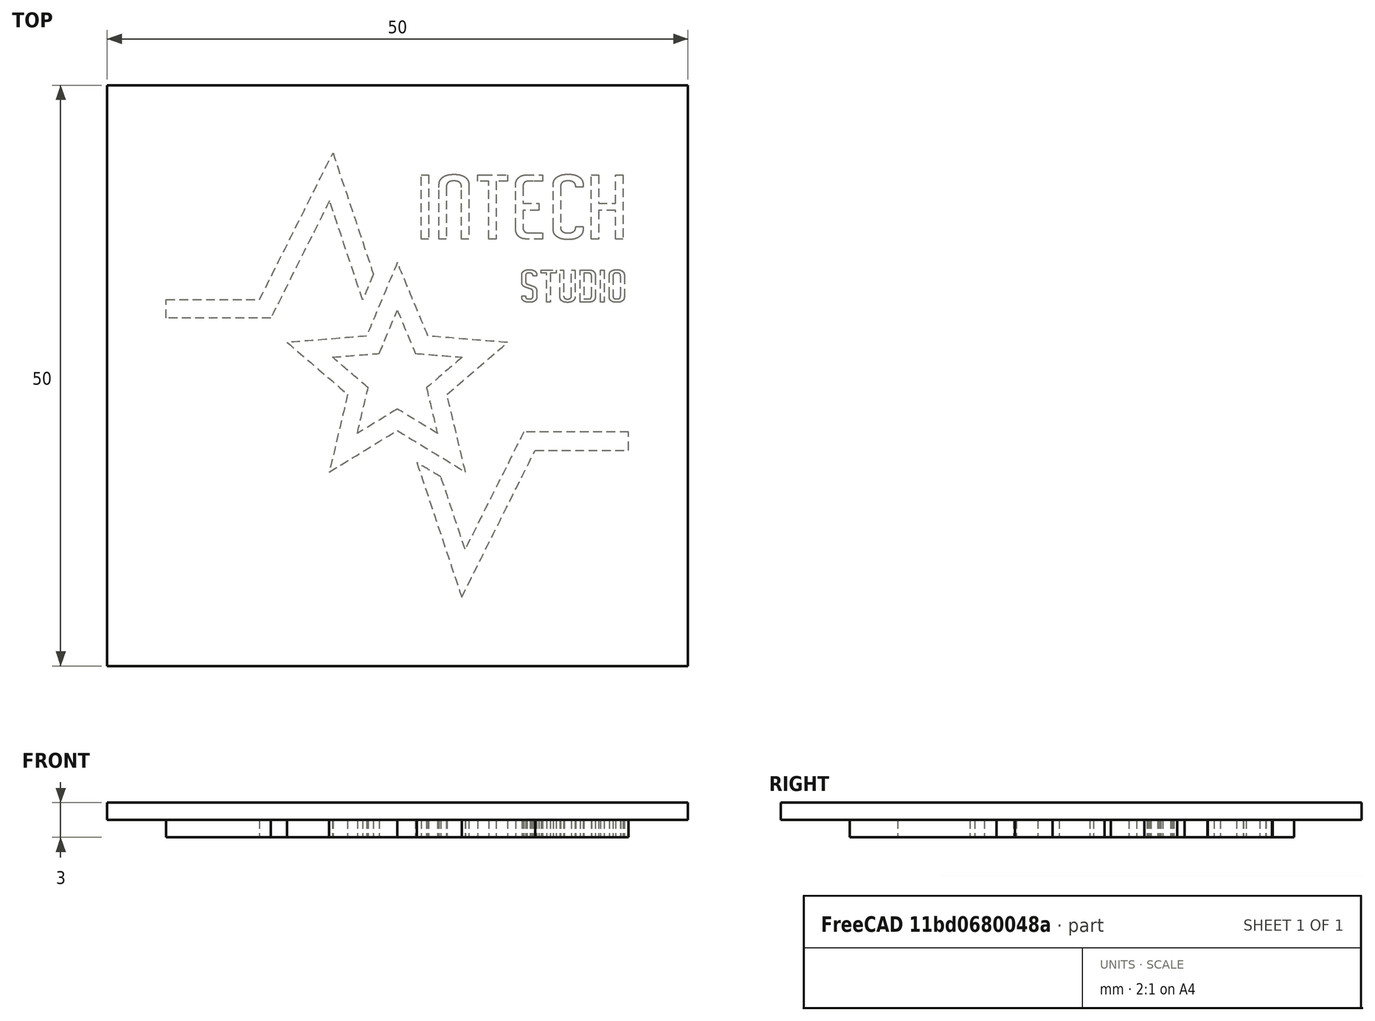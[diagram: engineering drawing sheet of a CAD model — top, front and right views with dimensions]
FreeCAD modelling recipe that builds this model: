
FCSTD DOCUMENT  (FreeCAD 0.18R16131 (Git))
Label: Intech Logo 5cm
License: All rights reserved
LicenseURL: http://en.wikipedia.org/wiki/All_rights_reserved
objects: Sketcher::SketchObject×2, PartDesign::Pad×2, PartDesign::Body×1
note: 7 computed .brp shape members not serialized (recipe doc carries the construction recipe); baked Part::Feature solids carry a one-line shape summary decoded from their .brp

FEATURE [Sketcher::SketchObject] Sketch018
  sketch-geometry (348):
    g0: BSplineCurve PolesCount=2 KnotsCount=2 Degree=1 IsPeriodic=0
    g1: BSplineCurve PolesCount=2 KnotsCount=2 Degree=1 IsPeriodic=0
    g2: BSplineCurve PolesCount=2 KnotsCount=2 Degree=1 IsPeriodic=0
    g3: BSplineCurve PolesCount=2 KnotsCount=2 Degree=1 IsPeriodic=0
    g4: BSplineCurve PolesCount=4 KnotsCount=2 Degree=3 IsPeriodic=0
    g5: BSplineCurve PolesCount=4 KnotsCount=2 Degree=3 IsPeriodic=0
    g6: BSplineCurve PolesCount=4 KnotsCount=2 Degree=3 IsPeriodic=0
    g7: BSplineCurve PolesCount=4 KnotsCount=2 Degree=3 IsPeriodic=0
    g8: BSplineCurve PolesCount=4 KnotsCount=2 Degree=3 IsPeriodic=0
    g9: BSplineCurve PolesCount=4 KnotsCount=2 Degree=3 IsPeriodic=0
    g10: BSplineCurve PolesCount=4 KnotsCount=2 Degree=3 IsPeriodic=0
    g11: BSplineCurve PolesCount=4 KnotsCount=2 Degree=3 IsPeriodic=0
    g12: BSplineCurve PolesCount=2 KnotsCount=2 Degree=1 IsPeriodic=0
    g13: BSplineCurve PolesCount=2 KnotsCount=2 Degree=1 IsPeriodic=0
    g14: BSplineCurve PolesCount=2 KnotsCount=2 Degree=1 IsPeriodic=0
    g15: BSplineCurve PolesCount=4 KnotsCount=2 Degree=3 IsPeriodic=0
    g16: BSplineCurve PolesCount=4 KnotsCount=2 Degree=3 IsPeriodic=0
    g17: BSplineCurve PolesCount=4 KnotsCount=2 Degree=3 IsPeriodic=0
    g18: BSplineCurve PolesCount=4 KnotsCount=2 Degree=3 IsPeriodic=0
    g19: BSplineCurve PolesCount=4 KnotsCount=2 Degree=3 IsPeriodic=0
    g20: BSplineCurve PolesCount=4 KnotsCount=2 Degree=3 IsPeriodic=0
    g21: BSplineCurve PolesCount=4 KnotsCount=2 Degree=3 IsPeriodic=0
    g22: BSplineCurve PolesCount=4 KnotsCount=2 Degree=3 IsPeriodic=0
    g23: BSplineCurve PolesCount=2 KnotsCount=2 Degree=1 IsPeriodic=0
    g24: BSplineCurve PolesCount=2 KnotsCount=2 Degree=1 IsPeriodic=0
    g25: BSplineCurve PolesCount=2 KnotsCount=2 Degree=1 IsPeriodic=0
    g26: BSplineCurve PolesCount=2 KnotsCount=2 Degree=1 IsPeriodic=0
    g27: BSplineCurve PolesCount=2 KnotsCount=2 Degree=1 IsPeriodic=0
    g28: BSplineCurve PolesCount=2 KnotsCount=2 Degree=1 IsPeriodic=0
    g29: BSplineCurve PolesCount=2 KnotsCount=2 Degree=1 IsPeriodic=0
    g30: BSplineCurve PolesCount=2 KnotsCount=2 Degree=1 IsPeriodic=0
    g31: BSplineCurve PolesCount=2 KnotsCount=2 Degree=1 IsPeriodic=0
    g32: BSplineCurve PolesCount=2 KnotsCount=2 Degree=1 IsPeriodic=0
    g33: BSplineCurve PolesCount=2 KnotsCount=2 Degree=1 IsPeriodic=0
    g34: BSplineCurve PolesCount=2 KnotsCount=2 Degree=1 IsPeriodic=0
    g35: BSplineCurve PolesCount=2 KnotsCount=2 Degree=1 IsPeriodic=0
    g36: BSplineCurve PolesCount=2 KnotsCount=2 Degree=1 IsPeriodic=0
    g37: BSplineCurve PolesCount=2 KnotsCount=2 Degree=1 IsPeriodic=0
    g38: BSplineCurve PolesCount=2 KnotsCount=2 Degree=1 IsPeriodic=0
    g39: BSplineCurve PolesCount=2 KnotsCount=2 Degree=1 IsPeriodic=0
    g40: BSplineCurve PolesCount=2 KnotsCount=2 Degree=1 IsPeriodic=0
    g41: BSplineCurve PolesCount=2 KnotsCount=2 Degree=1 IsPeriodic=0
    g42: BSplineCurve PolesCount=2 KnotsCount=2 Degree=1 IsPeriodic=0
    g43: BSplineCurve PolesCount=2 KnotsCount=2 Degree=1 IsPeriodic=0
    g44: BSplineCurve PolesCount=2 KnotsCount=2 Degree=1 IsPeriodic=0
    g45: BSplineCurve PolesCount=2 KnotsCount=2 Degree=1 IsPeriodic=0
    g46: BSplineCurve PolesCount=2 KnotsCount=2 Degree=1 IsPeriodic=0
    g47: BSplineCurve PolesCount=2 KnotsCount=2 Degree=1 IsPeriodic=0
    g48: BSplineCurve PolesCount=2 KnotsCount=2 Degree=1 IsPeriodic=0
    g49: BSplineCurve PolesCount=2 KnotsCount=2 Degree=1 IsPeriodic=0
    g50: BSplineCurve PolesCount=2 KnotsCount=2 Degree=1 IsPeriodic=0
    g51: BSplineCurve PolesCount=2 KnotsCount=2 Degree=1 IsPeriodic=0
    g52: BSplineCurve PolesCount=2 KnotsCount=2 Degree=1 IsPeriodic=0
    g53: BSplineCurve PolesCount=2 KnotsCount=2 Degree=1 IsPeriodic=0
    g54: BSplineCurve PolesCount=2 KnotsCount=2 Degree=1 IsPeriodic=0
    g55: BSplineCurve PolesCount=2 KnotsCount=2 Degree=1 IsPeriodic=0
    g56: BSplineCurve PolesCount=4 KnotsCount=2 Degree=3 IsPeriodic=0
    g57: BSplineCurve PolesCount=4 KnotsCount=2 Degree=3 IsPeriodic=0
    g58: BSplineCurve PolesCount=4 KnotsCount=2 Degree=3 IsPeriodic=0
    g59: BSplineCurve PolesCount=4 KnotsCount=2 Degree=3 IsPeriodic=0
    g60: BSplineCurve PolesCount=4 KnotsCount=2 Degree=3 IsPeriodic=0
    g61: BSplineCurve PolesCount=4 KnotsCount=2 Degree=3 IsPeriodic=0
    g62: BSplineCurve PolesCount=4 KnotsCount=2 Degree=3 IsPeriodic=0
    g63: BSplineCurve PolesCount=4 KnotsCount=2 Degree=3 IsPeriodic=0
    g64: BSplineCurve PolesCount=2 KnotsCount=2 Degree=1 IsPeriodic=0
    g65: BSplineCurve PolesCount=2 KnotsCount=2 Degree=1 IsPeriodic=0
    g66: BSplineCurve PolesCount=2 KnotsCount=2 Degree=1 IsPeriodic=0
    g67: BSplineCurve PolesCount=4 KnotsCount=2 Degree=3 IsPeriodic=0
    g68: BSplineCurve PolesCount=4 KnotsCount=2 Degree=3 IsPeriodic=0
    g69: BSplineCurve PolesCount=4 KnotsCount=2 Degree=3 IsPeriodic=0
    g70: BSplineCurve PolesCount=4 KnotsCount=2 Degree=3 IsPeriodic=0
    g71: BSplineCurve PolesCount=4 KnotsCount=2 Degree=3 IsPeriodic=0
    g72: BSplineCurve PolesCount=4 KnotsCount=2 Degree=3 IsPeriodic=0
    g73: BSplineCurve PolesCount=4 KnotsCount=2 Degree=3 IsPeriodic=0
    g74: BSplineCurve PolesCount=4 KnotsCount=2 Degree=3 IsPeriodic=0
    g75: BSplineCurve PolesCount=2 KnotsCount=2 Degree=1 IsPeriodic=0
    g76: BSplineCurve PolesCount=2 KnotsCount=2 Degree=1 IsPeriodic=0
    g77: BSplineCurve PolesCount=2 KnotsCount=2 Degree=1 IsPeriodic=0
    g78: BSplineCurve PolesCount=4 KnotsCount=2 Degree=3 IsPeriodic=0
    g79: BSplineCurve PolesCount=4 KnotsCount=2 Degree=3 IsPeriodic=0
    g80: BSplineCurve PolesCount=4 KnotsCount=2 Degree=3 IsPeriodic=0
    g81: BSplineCurve PolesCount=4 KnotsCount=2 Degree=3 IsPeriodic=0
    g82: BSplineCurve PolesCount=2 KnotsCount=2 Degree=1 IsPeriodic=0
    g83: BSplineCurve PolesCount=4 KnotsCount=2 Degree=3 IsPeriodic=0
    g84: BSplineCurve PolesCount=4 KnotsCount=2 Degree=3 IsPeriodic=0
    g85: BSplineCurve PolesCount=4 KnotsCount=2 Degree=3 IsPeriodic=0
    g86: BSplineCurve PolesCount=2 KnotsCount=2 Degree=1 IsPeriodic=0
    g87: BSplineCurve PolesCount=2 KnotsCount=2 Degree=1 IsPeriodic=0
    g88: BSplineCurve PolesCount=2 KnotsCount=2 Degree=1 IsPeriodic=0
    g89: BSplineCurve PolesCount=2 KnotsCount=2 Degree=1 IsPeriodic=0
    g90: BSplineCurve PolesCount=4 KnotsCount=2 Degree=3 IsPeriodic=0
    g91: BSplineCurve PolesCount=4 KnotsCount=2 Degree=3 IsPeriodic=0
    g92: BSplineCurve PolesCount=4 KnotsCount=2 Degree=3 IsPeriodic=0
    g93: BSplineCurve PolesCount=4 KnotsCount=2 Degree=3 IsPeriodic=0
    g94: BSplineCurve PolesCount=4 KnotsCount=2 Degree=3 IsPeriodic=0
    g95: BSplineCurve PolesCount=4 KnotsCount=2 Degree=3 IsPeriodic=0
    g96: BSplineCurve PolesCount=4 KnotsCount=2 Degree=3 IsPeriodic=0
    g97: BSplineCurve PolesCount=4 KnotsCount=2 Degree=3 IsPeriodic=0
    g98: BSplineCurve PolesCount=2 KnotsCount=2 Degree=1 IsPeriodic=0
    g99: BSplineCurve PolesCount=2 KnotsCount=2 Degree=1 IsPeriodic=0
    g100: BSplineCurve PolesCount=2 KnotsCount=2 Degree=1 IsPeriodic=0
    g101: BSplineCurve PolesCount=4 KnotsCount=2 Degree=3 IsPeriodic=0
    g102: BSplineCurve PolesCount=4 KnotsCount=2 Degree=3 IsPeriodic=0
    g103: BSplineCurve PolesCount=4 KnotsCount=2 Degree=3 IsPeriodic=0
    g104: BSplineCurve PolesCount=4 KnotsCount=2 Degree=3 IsPeriodic=0
    g105: BSplineCurve PolesCount=4 KnotsCount=2 Degree=3 IsPeriodic=0
    g106: BSplineCurve PolesCount=4 KnotsCount=2 Degree=3 IsPeriodic=0
    g107: BSplineCurve PolesCount=4 KnotsCount=2 Degree=3 IsPeriodic=0
    g108: BSplineCurve PolesCount=4 KnotsCount=2 Degree=3 IsPeriodic=0
    g109: BSplineCurve PolesCount=2 KnotsCount=2 Degree=1 IsPeriodic=0
    g110: BSplineCurve PolesCount=2 KnotsCount=2 Degree=1 IsPeriodic=0
    g111: BSplineCurve PolesCount=2 KnotsCount=2 Degree=1 IsPeriodic=0
    g112: BSplineCurve PolesCount=4 KnotsCount=2 Degree=3 IsPeriodic=0
    g113: BSplineCurve PolesCount=4 KnotsCount=2 Degree=3 IsPeriodic=0
    g114: BSplineCurve PolesCount=4 KnotsCount=2 Degree=3 IsPeriodic=0
    g115: BSplineCurve PolesCount=4 KnotsCount=2 Degree=3 IsPeriodic=0
    g116: BSplineCurve PolesCount=4 KnotsCount=2 Degree=3 IsPeriodic=0
    g117: BSplineCurve PolesCount=4 KnotsCount=2 Degree=3 IsPeriodic=0
    g118: BSplineCurve PolesCount=4 KnotsCount=2 Degree=3 IsPeriodic=0
    g119: BSplineCurve PolesCount=4 KnotsCount=2 Degree=3 IsPeriodic=0
    g120: BSplineCurve PolesCount=4 KnotsCount=2 Degree=3 IsPeriodic=0
    g121: BSplineCurve PolesCount=4 KnotsCount=2 Degree=3 IsPeriodic=0
    g122: BSplineCurve PolesCount=2 KnotsCount=2 Degree=1 IsPeriodic=0
    g123: BSplineCurve PolesCount=2 KnotsCount=2 Degree=1 IsPeriodic=0
    g124: BSplineCurve PolesCount=2 KnotsCount=2 Degree=1 IsPeriodic=0
    g125: BSplineCurve PolesCount=2 KnotsCount=2 Degree=1 IsPeriodic=0
    g126: BSplineCurve PolesCount=2 KnotsCount=2 Degree=1 IsPeriodic=0
    g127: BSplineCurve PolesCount=2 KnotsCount=2 Degree=1 IsPeriodic=0
    g128: BSplineCurve PolesCount=4 KnotsCount=2 Degree=3 IsPeriodic=0
    g129: BSplineCurve PolesCount=4 KnotsCount=2 Degree=3 IsPeriodic=0
    g130: BSplineCurve PolesCount=4 KnotsCount=2 Degree=3 IsPeriodic=0
    g131: BSplineCurve PolesCount=4 KnotsCount=2 Degree=3 IsPeriodic=0
    g132: BSplineCurve PolesCount=4 KnotsCount=2 Degree=3 IsPeriodic=0
    g133: BSplineCurve PolesCount=4 KnotsCount=2 Degree=3 IsPeriodic=0
    g134: BSplineCurve PolesCount=4 KnotsCount=2 Degree=3 IsPeriodic=0
    g135: BSplineCurve PolesCount=4 KnotsCount=2 Degree=3 IsPeriodic=0
    g136: BSplineCurve PolesCount=2 KnotsCount=2 Degree=1 IsPeriodic=0
    g137: BSplineCurve PolesCount=2 KnotsCount=2 Degree=1 IsPeriodic=0
    g138: BSplineCurve PolesCount=2 KnotsCount=2 Degree=1 IsPeriodic=0
    g139: BSplineCurve PolesCount=2 KnotsCount=2 Degree=1 IsPeriodic=0
    g140: BSplineCurve PolesCount=2 KnotsCount=2 Degree=1 IsPeriodic=0
    g141: BSplineCurve PolesCount=4 KnotsCount=2 Degree=3 IsPeriodic=0
    g142: BSplineCurve PolesCount=4 KnotsCount=2 Degree=3 IsPeriodic=0
    g143: BSplineCurve PolesCount=4 KnotsCount=2 Degree=3 IsPeriodic=0
    g144: BSplineCurve PolesCount=4 KnotsCount=2 Degree=3 IsPeriodic=0
    g145: BSplineCurve PolesCount=4 KnotsCount=2 Degree=3 IsPeriodic=0
    g146: BSplineCurve PolesCount=4 KnotsCount=2 Degree=3 IsPeriodic=0
    g147: BSplineCurve PolesCount=4 KnotsCount=2 Degree=3 IsPeriodic=0
    g148: BSplineCurve PolesCount=4 KnotsCount=2 Degree=3 IsPeriodic=0
    g149: BSplineCurve PolesCount=2 KnotsCount=2 Degree=1 IsPeriodic=0
    g150: BSplineCurve PolesCount=2 KnotsCount=2 Degree=1 IsPeriodic=0
    g151: BSplineCurve PolesCount=2 KnotsCount=2 Degree=1 IsPeriodic=0
    g152: BSplineCurve PolesCount=2 KnotsCount=2 Degree=1 IsPeriodic=0
    g153: BSplineCurve PolesCount=2 KnotsCount=2 Degree=1 IsPeriodic=0
    g154: BSplineCurve PolesCount=2 KnotsCount=2 Degree=1 IsPeriodic=0
    g155: BSplineCurve PolesCount=2 KnotsCount=2 Degree=1 IsPeriodic=0
    g156: BSplineCurve PolesCount=2 KnotsCount=2 Degree=1 IsPeriodic=0
    g157: BSplineCurve PolesCount=2 KnotsCount=2 Degree=1 IsPeriodic=0
    g158: BSplineCurve PolesCount=2 KnotsCount=2 Degree=1 IsPeriodic=0
    g159: BSplineCurve PolesCount=2 KnotsCount=2 Degree=1 IsPeriodic=0
    g160: BSplineCurve PolesCount=2 KnotsCount=2 Degree=1 IsPeriodic=0
    g161: BSplineCurve PolesCount=2 KnotsCount=2 Degree=1 IsPeriodic=0
    g162: BSplineCurve PolesCount=2 KnotsCount=2 Degree=1 IsPeriodic=0
    g163: BSplineCurve PolesCount=2 KnotsCount=2 Degree=1 IsPeriodic=0
    g164: BSplineCurve PolesCount=4 KnotsCount=2 Degree=3 IsPeriodic=0
    g165: BSplineCurve PolesCount=4 KnotsCount=2 Degree=3 IsPeriodic=0
    g166: BSplineCurve PolesCount=4 KnotsCount=2 Degree=3 IsPeriodic=0
    g167: BSplineCurve PolesCount=4 KnotsCount=2 Degree=3 IsPeriodic=0
    g168: BSplineCurve PolesCount=4 KnotsCount=2 Degree=3 IsPeriodic=0
    g169: BSplineCurve PolesCount=4 KnotsCount=2 Degree=3 IsPeriodic=0
    g170: BSplineCurve PolesCount=4 KnotsCount=2 Degree=3 IsPeriodic=0
    g171: BSplineCurve PolesCount=4 KnotsCount=2 Degree=3 IsPeriodic=0
    g172: BSplineCurve PolesCount=2 KnotsCount=2 Degree=1 IsPeriodic=0
    g173: BSplineCurve PolesCount=2 KnotsCount=2 Degree=1 IsPeriodic=0
    g174: BSplineCurve PolesCount=2 KnotsCount=2 Degree=1 IsPeriodic=0
    g175: BSplineCurve PolesCount=2 KnotsCount=2 Degree=1 IsPeriodic=0
    g176: BSplineCurve PolesCount=2 KnotsCount=2 Degree=1 IsPeriodic=0
    g177: BSplineCurve PolesCount=4 KnotsCount=2 Degree=3 IsPeriodic=0
    g178: BSplineCurve PolesCount=4 KnotsCount=2 Degree=3 IsPeriodic=0
    g179: BSplineCurve PolesCount=4 KnotsCount=2 Degree=3 IsPeriodic=0
    g180: BSplineCurve PolesCount=4 KnotsCount=2 Degree=3 IsPeriodic=0
    g181: BSplineCurve PolesCount=4 KnotsCount=2 Degree=3 IsPeriodic=0
    g182: BSplineCurve PolesCount=4 KnotsCount=2 Degree=3 IsPeriodic=0
    g183: BSplineCurve PolesCount=4 KnotsCount=2 Degree=3 IsPeriodic=0
    g184: BSplineCurve PolesCount=4 KnotsCount=2 Degree=3 IsPeriodic=0
    g185: BSplineCurve PolesCount=2 KnotsCount=2 Degree=1 IsPeriodic=0
    g186: BSplineCurve PolesCount=2 KnotsCount=2 Degree=1 IsPeriodic=0
    g187: BSplineCurve PolesCount=2 KnotsCount=2 Degree=1 IsPeriodic=0
    g188: BSplineCurve PolesCount=2 KnotsCount=2 Degree=1 IsPeriodic=0
    g189: BSplineCurve PolesCount=2 KnotsCount=2 Degree=1 IsPeriodic=0
    g190: BSplineCurve PolesCount=4 KnotsCount=2 Degree=3 IsPeriodic=0
    g191: BSplineCurve PolesCount=4 KnotsCount=2 Degree=3 IsPeriodic=0
    g192: BSplineCurve PolesCount=4 KnotsCount=2 Degree=3 IsPeriodic=0
    g193: BSplineCurve PolesCount=4 KnotsCount=2 Degree=3 IsPeriodic=0
    g194: BSplineCurve PolesCount=2 KnotsCount=2 Degree=1 IsPeriodic=0
    g195: BSplineCurve PolesCount=2 KnotsCount=2 Degree=1 IsPeriodic=0
    g196: BSplineCurve PolesCount=2 KnotsCount=2 Degree=1 IsPeriodic=0
    g197: BSplineCurve PolesCount=4 KnotsCount=2 Degree=3 IsPeriodic=0
    g198: BSplineCurve PolesCount=4 KnotsCount=2 Degree=3 IsPeriodic=0
    g199: BSplineCurve PolesCount=4 KnotsCount=2 Degree=3 IsPeriodic=0
    g200: BSplineCurve PolesCount=4 KnotsCount=2 Degree=3 IsPeriodic=0
    g201: BSplineCurve PolesCount=2 KnotsCount=2 Degree=1 IsPeriodic=0
    g202: BSplineCurve PolesCount=2 KnotsCount=2 Degree=1 IsPeriodic=0
    g203: BSplineCurve PolesCount=2 KnotsCount=2 Degree=1 IsPeriodic=0
    g204: BSplineCurve PolesCount=2 KnotsCount=2 Degree=1 IsPeriodic=0
    g205: BSplineCurve PolesCount=4 KnotsCount=2 Degree=3 IsPeriodic=0
    g206: BSplineCurve PolesCount=4 KnotsCount=2 Degree=3 IsPeriodic=0
    g207: BSplineCurve PolesCount=2 KnotsCount=2 Degree=1 IsPeriodic=0
    g208: BSplineCurve PolesCount=2 KnotsCount=2 Degree=1 IsPeriodic=0
    g209: BSplineCurve PolesCount=2 KnotsCount=2 Degree=1 IsPeriodic=0
    g210: BSplineCurve PolesCount=2 KnotsCount=2 Degree=1 IsPeriodic=0
    g211: BSplineCurve PolesCount=2 KnotsCount=2 Degree=1 IsPeriodic=0
    g212: BSplineCurve PolesCount=2 KnotsCount=2 Degree=1 IsPeriodic=0
    g213: BSplineCurve PolesCount=2 KnotsCount=2 Degree=1 IsPeriodic=0
    g214: BSplineCurve PolesCount=4 KnotsCount=2 Degree=3 IsPeriodic=0
    g215: BSplineCurve PolesCount=4 KnotsCount=2 Degree=3 IsPeriodic=0
    g216: BSplineCurve PolesCount=2 KnotsCount=2 Degree=1 IsPeriodic=0
    g217: BSplineCurve PolesCount=2 KnotsCount=2 Degree=1 IsPeriodic=0
    g218: BSplineCurve PolesCount=2 KnotsCount=2 Degree=1 IsPeriodic=0
    g219: BSplineCurve PolesCount=2 KnotsCount=2 Degree=1 IsPeriodic=0
    g220: BSplineCurve PolesCount=2 KnotsCount=2 Degree=1 IsPeriodic=0
    g221: BSplineCurve PolesCount=2 KnotsCount=2 Degree=1 IsPeriodic=0
    g222: BSplineCurve PolesCount=2 KnotsCount=2 Degree=1 IsPeriodic=0
    g223: BSplineCurve PolesCount=2 KnotsCount=2 Degree=1 IsPeriodic=0
    g224: BSplineCurve PolesCount=4 KnotsCount=2 Degree=3 IsPeriodic=0
    g225: BSplineCurve PolesCount=4 KnotsCount=2 Degree=3 IsPeriodic=0
    g226: BSplineCurve PolesCount=4 KnotsCount=2 Degree=3 IsPeriodic=0
    g227: BSplineCurve PolesCount=4 KnotsCount=2 Degree=3 IsPeriodic=0
    g228: BSplineCurve PolesCount=4 KnotsCount=2 Degree=3 IsPeriodic=0
    g229: BSplineCurve PolesCount=4 KnotsCount=2 Degree=3 IsPeriodic=0
    g230: BSplineCurve PolesCount=4 KnotsCount=2 Degree=3 IsPeriodic=0
    g231: BSplineCurve PolesCount=4 KnotsCount=2 Degree=3 IsPeriodic=0
    g232: BSplineCurve PolesCount=2 KnotsCount=2 Degree=1 IsPeriodic=0
    g233: BSplineCurve PolesCount=2 KnotsCount=2 Degree=1 IsPeriodic=0
    g234: BSplineCurve PolesCount=2 KnotsCount=2 Degree=1 IsPeriodic=0
    g235: BSplineCurve PolesCount=4 KnotsCount=2 Degree=3 IsPeriodic=0
    g236: BSplineCurve PolesCount=4 KnotsCount=2 Degree=3 IsPeriodic=0
    g237: BSplineCurve PolesCount=4 KnotsCount=2 Degree=3 IsPeriodic=0
    g238: BSplineCurve PolesCount=4 KnotsCount=2 Degree=3 IsPeriodic=0
    g239: BSplineCurve PolesCount=4 KnotsCount=2 Degree=3 IsPeriodic=0
    g240: BSplineCurve PolesCount=4 KnotsCount=2 Degree=3 IsPeriodic=0
    g241: BSplineCurve PolesCount=4 KnotsCount=2 Degree=3 IsPeriodic=0
    g242: BSplineCurve PolesCount=4 KnotsCount=2 Degree=3 IsPeriodic=0
    g243: BSplineCurve PolesCount=2 KnotsCount=2 Degree=1 IsPeriodic=0
    g244: BSplineCurve PolesCount=2 KnotsCount=2 Degree=1 IsPeriodic=0
    g245: BSplineCurve PolesCount=2 KnotsCount=2 Degree=1 IsPeriodic=0
    g246: BSplineCurve PolesCount=4 KnotsCount=2 Degree=3 IsPeriodic=0
    g247: BSplineCurve PolesCount=4 KnotsCount=2 Degree=3 IsPeriodic=0
    g248: BSplineCurve PolesCount=4 KnotsCount=2 Degree=3 IsPeriodic=0
    g249: BSplineCurve PolesCount=4 KnotsCount=2 Degree=3 IsPeriodic=0
    g250: BSplineCurve PolesCount=4 KnotsCount=2 Degree=3 IsPeriodic=0
    g251: BSplineCurve PolesCount=4 KnotsCount=2 Degree=3 IsPeriodic=0
    g252: BSplineCurve PolesCount=4 KnotsCount=2 Degree=3 IsPeriodic=0
    g253: BSplineCurve PolesCount=4 KnotsCount=2 Degree=3 IsPeriodic=0
    g254: BSplineCurve PolesCount=2 KnotsCount=2 Degree=1 IsPeriodic=0
    g255: BSplineCurve PolesCount=2 KnotsCount=2 Degree=1 IsPeriodic=0
    g256: BSplineCurve PolesCount=2 KnotsCount=2 Degree=1 IsPeriodic=0
    g257: BSplineCurve PolesCount=4 KnotsCount=2 Degree=3 IsPeriodic=0
    g258: BSplineCurve PolesCount=4 KnotsCount=2 Degree=3 IsPeriodic=0
    g259: BSplineCurve PolesCount=4 KnotsCount=2 Degree=3 IsPeriodic=0
    g260: BSplineCurve PolesCount=4 KnotsCount=2 Degree=3 IsPeriodic=0
    g261: BSplineCurve PolesCount=4 KnotsCount=2 Degree=3 IsPeriodic=0
    g262: BSplineCurve PolesCount=4 KnotsCount=2 Degree=3 IsPeriodic=0
    g263: BSplineCurve PolesCount=4 KnotsCount=2 Degree=3 IsPeriodic=0
    g264: BSplineCurve PolesCount=4 KnotsCount=2 Degree=3 IsPeriodic=0
    g265: BSplineCurve PolesCount=2 KnotsCount=2 Degree=1 IsPeriodic=0
    g266: BSplineCurve PolesCount=2 KnotsCount=2 Degree=1 IsPeriodic=0
    g267: BSplineCurve PolesCount=2 KnotsCount=2 Degree=1 IsPeriodic=0
    g268: BSplineCurve PolesCount=2 KnotsCount=2 Degree=1 IsPeriodic=0
    g269: BSplineCurve PolesCount=2 KnotsCount=2 Degree=1 IsPeriodic=0
    g270: BSplineCurve PolesCount=2 KnotsCount=2 Degree=1 IsPeriodic=0
    g271: BSplineCurve PolesCount=2 KnotsCount=2 Degree=1 IsPeriodic=0
    g272: BSplineCurve PolesCount=2 KnotsCount=2 Degree=1 IsPeriodic=0
    g273: BSplineCurve PolesCount=2 KnotsCount=2 Degree=1 IsPeriodic=0
    g274: BSplineCurve PolesCount=2 KnotsCount=2 Degree=1 IsPeriodic=0
    g275: BSplineCurve PolesCount=2 KnotsCount=2 Degree=1 IsPeriodic=0
    g276: BSplineCurve PolesCount=2 KnotsCount=2 Degree=1 IsPeriodic=0
    g277: BSplineCurve PolesCount=2 KnotsCount=2 Degree=1 IsPeriodic=0
    g278: BSplineCurve PolesCount=2 KnotsCount=2 Degree=1 IsPeriodic=0
    g279: BSplineCurve PolesCount=2 KnotsCount=2 Degree=1 IsPeriodic=0
    g280: BSplineCurve PolesCount=2 KnotsCount=2 Degree=1 IsPeriodic=0
    g281: BSplineCurve PolesCount=2 KnotsCount=2 Degree=1 IsPeriodic=0
    g282: BSplineCurve PolesCount=2 KnotsCount=2 Degree=1 IsPeriodic=0
    g283: BSplineCurve PolesCount=2 KnotsCount=2 Degree=1 IsPeriodic=0
    g284: BSplineCurve PolesCount=2 KnotsCount=2 Degree=1 IsPeriodic=0
    g285: BSplineCurve PolesCount=2 KnotsCount=2 Degree=1 IsPeriodic=0
    g286: BSplineCurve PolesCount=2 KnotsCount=2 Degree=1 IsPeriodic=0
    g287: BSplineCurve PolesCount=2 KnotsCount=2 Degree=1 IsPeriodic=0
    g288: BSplineCurve PolesCount=2 KnotsCount=2 Degree=1 IsPeriodic=0
    g289: BSplineCurve PolesCount=4 KnotsCount=2 Degree=3 IsPeriodic=0
    g290: BSplineCurve PolesCount=4 KnotsCount=2 Degree=3 IsPeriodic=0
    g291: BSplineCurve PolesCount=4 KnotsCount=2 Degree=3 IsPeriodic=0
    g292: BSplineCurve PolesCount=4 KnotsCount=2 Degree=3 IsPeriodic=0
    g293: BSplineCurve PolesCount=2 KnotsCount=2 Degree=1 IsPeriodic=0
    g294: BSplineCurve PolesCount=2 KnotsCount=2 Degree=1 IsPeriodic=0
    g295: BSplineCurve PolesCount=2 KnotsCount=2 Degree=1 IsPeriodic=0
    g296: BSplineCurve PolesCount=2 KnotsCount=2 Degree=1 IsPeriodic=0
    g297: BSplineCurve PolesCount=2 KnotsCount=2 Degree=1 IsPeriodic=0
    g298: BSplineCurve PolesCount=2 KnotsCount=2 Degree=1 IsPeriodic=0
    g299: BSplineCurve PolesCount=4 KnotsCount=2 Degree=3 IsPeriodic=0
    g300: BSplineCurve PolesCount=4 KnotsCount=2 Degree=3 IsPeriodic=0
    g301: BSplineCurve PolesCount=4 KnotsCount=2 Degree=3 IsPeriodic=0
    g302: BSplineCurve PolesCount=4 KnotsCount=2 Degree=3 IsPeriodic=0
    g303: BSplineCurve PolesCount=2 KnotsCount=2 Degree=1 IsPeriodic=0
    g304: BSplineCurve PolesCount=2 KnotsCount=2 Degree=1 IsPeriodic=0
    g305: BSplineCurve PolesCount=2 KnotsCount=2 Degree=1 IsPeriodic=0
    g306: BSplineCurve PolesCount=2 KnotsCount=2 Degree=1 IsPeriodic=0
    g307: BSplineCurve PolesCount=4 KnotsCount=2 Degree=3 IsPeriodic=0
    g308: BSplineCurve PolesCount=4 KnotsCount=2 Degree=3 IsPeriodic=0
    g309: BSplineCurve PolesCount=4 KnotsCount=2 Degree=3 IsPeriodic=0
    g310: BSplineCurve PolesCount=4 KnotsCount=2 Degree=3 IsPeriodic=0
    g311: BSplineCurve PolesCount=4 KnotsCount=2 Degree=3 IsPeriodic=0
    g312: BSplineCurve PolesCount=4 KnotsCount=2 Degree=3 IsPeriodic=0
    g313: BSplineCurve PolesCount=4 KnotsCount=2 Degree=3 IsPeriodic=0
    g314: BSplineCurve PolesCount=4 KnotsCount=2 Degree=3 IsPeriodic=0
    g315: BSplineCurve PolesCount=2 KnotsCount=2 Degree=1 IsPeriodic=0
    g316: BSplineCurve PolesCount=2 KnotsCount=2 Degree=1 IsPeriodic=0
    g317: BSplineCurve PolesCount=2 KnotsCount=2 Degree=1 IsPeriodic=0
    g318: BSplineCurve PolesCount=4 KnotsCount=2 Degree=3 IsPeriodic=0
    g319: BSplineCurve PolesCount=4 KnotsCount=2 Degree=3 IsPeriodic=0
    g320: BSplineCurve PolesCount=4 KnotsCount=2 Degree=3 IsPeriodic=0
    g321: BSplineCurve PolesCount=4 KnotsCount=2 Degree=3 IsPeriodic=0
    g322: BSplineCurve PolesCount=4 KnotsCount=2 Degree=3 IsPeriodic=0
    g323: BSplineCurve PolesCount=4 KnotsCount=2 Degree=3 IsPeriodic=0
    g324: BSplineCurve PolesCount=4 KnotsCount=2 Degree=3 IsPeriodic=0
    g325: BSplineCurve PolesCount=4 KnotsCount=2 Degree=3 IsPeriodic=0
    g326: BSplineCurve PolesCount=2 KnotsCount=2 Degree=1 IsPeriodic=0
    g327: BSplineCurve PolesCount=2 KnotsCount=2 Degree=1 IsPeriodic=0
    g328: BSplineCurve PolesCount=2 KnotsCount=2 Degree=1 IsPeriodic=0
    g329: BSplineCurve PolesCount=4 KnotsCount=2 Degree=3 IsPeriodic=0
    g330: BSplineCurve PolesCount=4 KnotsCount=2 Degree=3 IsPeriodic=0
    g331: BSplineCurve PolesCount=2 KnotsCount=2 Degree=1 IsPeriodic=0
    g332: BSplineCurve PolesCount=2 KnotsCount=2 Degree=1 IsPeriodic=0
    g333: BSplineCurve PolesCount=2 KnotsCount=2 Degree=1 IsPeriodic=0
    g334: BSplineCurve PolesCount=2 KnotsCount=2 Degree=1 IsPeriodic=0
    g335: BSplineCurve PolesCount=2 KnotsCount=2 Degree=1 IsPeriodic=0
    g336: BSplineCurve PolesCount=4 KnotsCount=2 Degree=3 IsPeriodic=0
    g337: BSplineCurve PolesCount=4 KnotsCount=2 Degree=3 IsPeriodic=0
    g338: BSplineCurve PolesCount=2 KnotsCount=2 Degree=1 IsPeriodic=0
    g339: BSplineCurve PolesCount=2 KnotsCount=2 Degree=1 IsPeriodic=0
    g340: BSplineCurve PolesCount=2 KnotsCount=2 Degree=1 IsPeriodic=0
    g341: BSplineCurve PolesCount=2 KnotsCount=2 Degree=1 IsPeriodic=0
    g342: BSplineCurve PolesCount=2 KnotsCount=2 Degree=1 IsPeriodic=0
    g343: BSplineCurve PolesCount=2 KnotsCount=2 Degree=1 IsPeriodic=0
    g344: BSplineCurve PolesCount=2 KnotsCount=2 Degree=1 IsPeriodic=0
    g345: BSplineCurve PolesCount=2 KnotsCount=2 Degree=1 IsPeriodic=0
    g346: BSplineCurve PolesCount=2 KnotsCount=2 Degree=1 IsPeriodic=0
    g347: BSplineCurve PolesCount=2 KnotsCount=2 Degree=1 IsPeriodic=0
  constraints (348):
    c: Coincident(g0,g1)
    c: Coincident(g1,g2)
    c: Coincident(g2,g3)
    c: Coincident(g3,g4)
    c: Coincident(g4,g5)
    c: Coincident(g5,g6)
    c: Coincident(g6,g7)
    c: Coincident(g7,g8)
    c: Coincident(g8,g9)
    c: Coincident(g9,g10)
    c: Coincident(g10,g11)
    c: Coincident(g11,g12)
    c: Coincident(g12,g13)
    c: Coincident(g13,g14)
    c: Coincident(g14,g15)
    c: Coincident(g15,g16)
    c: Coincident(g16,g17)
    c: Coincident(g17,g18)
    c: Coincident(g18,g19)
    c: Coincident(g19,g20)
    c: Coincident(g20,g21)
    c: Coincident(g21,g22)
    c: Coincident(g22,g23)
    c: Coincident(g23,g0)
    c: Coincident(g24,g25)
    c: Coincident(g25,g26)
    c: Coincident(g26,g27)
    c: Coincident(g27,g28)
    c: Coincident(g28,g29)
    c: Coincident(g29,g30)
    c: Coincident(g30,g31)
    c: Coincident(g31,g24)
    c: Coincident(g32,g33)
    c: Coincident(g33,g34)
    c: Coincident(g34,g35)
    c: Coincident(g35,g36)
    c: Coincident(g36,g37)
    c: Coincident(g37,g38)
    c: Coincident(g38,g39)
    c: Coincident(g39,g40)
    c: Coincident(g40,g41)
    c: Coincident(g41,g32)
    c: Coincident(g42,g43)
    c: Coincident(g43,g44)
    c: Coincident(g44,g45)
    c: Coincident(g45,g46)
    c: Coincident(g46,g47)
    c: Coincident(g47,g48)
    c: Coincident(g48,g49)
    c: Coincident(g49,g50)
    c: Coincident(g50,g51)
    c: Coincident(g51,g42)
    c: Coincident(g52,g53)
    c: Coincident(g53,g54)
    c: Coincident(g54,g55)
    c: Coincident(g55,g52)
    c: Coincident(g56,g57)
    c: Coincident(g57,g58)
    c: Coincident(g58,g59)
    c: Coincident(g59,g60)
    c: Coincident(g60,g61)
    c: Coincident(g61,g62)
    c: Coincident(g62,g63)
    c: Coincident(g63,g64)
    c: Coincident(g64,g65)
    c: Coincident(g65,g66)
    c: Coincident(g66,g67)
    c: Coincident(g67,g68)
    c: Coincident(g68,g69)
    c: Coincident(g69,g70)
    c: Coincident(g70,g71)
    c: Coincident(g71,g72)
    c: Coincident(g72,g73)
    c: Coincident(g73,g74)
    c: Coincident(g74,g75)
    c: Coincident(g75,g76)
    c: Coincident(g76,g77)
    c: Coincident(g77,g78)
    c: Coincident(g78,g79)
    c: Coincident(g79,g80)
    c: Coincident(g80,g81)
    c: Coincident(g81,g82)
    c: Coincident(g82,g83)
    c: Coincident(g83,g84)
    c: Coincident(g84,g85)
    c: Coincident(g85,g86)
    c: Coincident(g86,g87)
    c: Coincident(g87,g88)
    c: Coincident(g88,g89)
    c: Coincident(g89,g90)
    c: Coincident(g90,g91)
    c: Coincident(g91,g92)
    c: Coincident(g92,g93)
    c: Coincident(g93,g94)
    c: Coincident(g94,g95)
    c: Coincident(g95,g96)
    c: Coincident(g96,g97)
    c: Coincident(g97,g98)
    c: Coincident(g98,g99)
    c: Coincident(g99,g100)
    c: Coincident(g100,g101)
    c: Coincident(g101,g102)
    c: Coincident(g102,g103)
    c: Coincident(g103,g104)
    c: Coincident(g104,g105)
    c: Coincident(g105,g106)
    c: Coincident(g106,g107)
    c: Coincident(g107,g108)
    c: Coincident(g108,g109)
    c: Coincident(g109,g110)
    c: Coincident(g110,g111)
    c: Coincident(g111,g112)
    c: Coincident(g112,g113)
    c: Coincident(g113,g114)
    c: Coincident(g114,g115)
    c: Coincident(g115,g116)
    c: Coincident(g116,g117)
    c: Coincident(g117,g118)
    c: Coincident(g118,g119)
    c: Coincident(g119,g120)
    c: Coincident(g120,g121)
    c: Coincident(g121,g122)
    c: Coincident(g122,g123)
    c: Coincident(g123,g124)
    c: Coincident(g124,g56)
    c: Coincident(g125,g126)
    c: Coincident(g126,g127)
    c: Coincident(g127,g128)
    c: Coincident(g128,g129)
    c: Coincident(g129,g130)
    c: Coincident(g130,g131)
    c: Coincident(g131,g132)
    c: Coincident(g132,g133)
    c: Coincident(g133,g134)
    c: Coincident(g134,g135)
    c: Coincident(g135,g136)
    c: Coincident(g136,g137)
    c: Coincident(g137,g138)
    c: Coincident(g138,g139)
    c: Coincident(g139,g140)
    c: Coincident(g140,g141)
    c: Coincident(g141,g142)
    c: Coincident(g142,g143)
    c: Coincident(g143,g144)
    c: Coincident(g144,g145)
    c: Coincident(g145,g146)
    c: Coincident(g146,g147)
    c: Coincident(g147,g148)
    c: Coincident(g148,g149)
    c: Coincident(g149,g150)
    c: Coincident(g150,g151)
    c: Coincident(g151,g125)
    c: Coincident(g152,g153)
    c: Coincident(g153,g154)
    c: Coincident(g154,g155)
    c: Coincident(g155,g156)
    c: Coincident(g156,g157)
    c: Coincident(g157,g158)
    c: Coincident(g158,g159)
    c: Coincident(g159,g160)
    c: Coincident(g160,g161)
    c: Coincident(g161,g152)
    c: Coincident(g162,g163)
    c: Coincident(g163,g164)
    c: Coincident(g164,g165)
    c: Coincident(g165,g166)
    c: Coincident(g166,g167)
    c: Coincident(g167,g168)
    c: Coincident(g168,g169)
    c: Coincident(g169,g170)
    c: Coincident(g170,g171)
    c: Coincident(g171,g172)
    c: Coincident(g172,g173)
    c: Coincident(g173,g174)
    c: Coincident(g174,g175)
    c: Coincident(g175,g176)
    c: Coincident(g176,g177)
    c: Coincident(g177,g178)
    c: Coincident(g178,g179)
    c: Coincident(g179,g180)
    c: Coincident(g180,g181)
    c: Coincident(g181,g182)
    c: Coincident(g182,g183)
    c: Coincident(g183,g184)
    c: Coincident(g184,g185)
    c: Coincident(g185,g186)
    c: Coincident(g186,g187)
    c: Coincident(g187,g188)
    c: Coincident(g188,g162)
    c: Coincident(g189,g190)
    c: Coincident(g190,g191)
    c: Coincident(g191,g192)
    c: Coincident(g192,g193)
    c: Coincident(g193,g194)
    c: Coincident(g194,g195)
    c: Coincident(g195,g196)
    c: Coincident(g196,g197)
    c: Coincident(g197,g198)
    c: Coincident(g198,g199)
    c: Coincident(g199,g200)
    c: Coincident(g200,g201)
    c: Coincident(g201,g202)
    c: Coincident(g202,g203)
    c: Coincident(g203,g204)
    c: Coincident(g204,g205)
    c: Coincident(g205,g206)
    c: Coincident(g206,g207)
    c: Coincident(g207,g208)
    c: Coincident(g208,g209)
    c: Coincident(g209,g210)
    c: Coincident(g210,g211)
    c: Coincident(g211,g212)
    c: Coincident(g212,g213)
    c: Coincident(g213,g214)
    c: Coincident(g214,g215)
    c: Coincident(g215,g216)
    c: Coincident(g216,g217)
    c: Coincident(g217,g218)
    c: Coincident(g218,g189)
    c: Coincident(g219,g220)
    c: Coincident(g220,g221)
    c: Coincident(g221,g222)
    c: Coincident(g222,g219)
    c: Coincident(g223,g224)
    c: Coincident(g224,g225)
    c: Coincident(g225,g226)
    c: Coincident(g226,g227)
    c: Coincident(g227,g228)
    c: Coincident(g228,g229)
    c: Coincident(g229,g230)
    c: Coincident(g230,g231)
    c: Coincident(g231,g232)
    c: Coincident(g232,g233)
    c: Coincident(g233,g234)
    c: Coincident(g234,g235)
    c: Coincident(g235,g236)
    c: Coincident(g236,g237)
    c: Coincident(g237,g238)
    c: Coincident(g238,g239)
    c: Coincident(g239,g240)
    c: Coincident(g240,g241)
    c: Coincident(g241,g242)
    c: Coincident(g242,g243)
    c: Coincident(g243,g244)
    c: Coincident(g244,g245)
    c: Coincident(g245,g246)
    c: Coincident(g246,g247)
    c: Coincident(g247,g248)
    c: Coincident(g248,g249)
    c: Coincident(g249,g250)
    c: Coincident(g250,g251)
    c: Coincident(g251,g252)
    c: Coincident(g252,g253)
    c: Coincident(g253,g254)
    c: Coincident(g254,g255)
    c: Coincident(g255,g256)
    c: Coincident(g256,g257)
    c: Coincident(g257,g258)
    c: Coincident(g258,g259)
    c: Coincident(g259,g260)
    c: Coincident(g260,g261)
    c: Coincident(g261,g262)
    c: Coincident(g262,g263)
    c: Coincident(g263,g264)
    c: Coincident(g264,g265)
    c: Coincident(g265,g266)
    c: Coincident(g266,g223)
    c: Coincident(g267,g268)
    c: Coincident(g268,g269)
    c: Coincident(g269,g270)
    c: Coincident(g270,g271)
    c: Coincident(g271,g272)
    c: Coincident(g272,g273)
    c: Coincident(g273,g274)
    c: Coincident(g274,g275)
    c: Coincident(g275,g276)
    c: Coincident(g276,g277)
    c: Coincident(g277,g278)
    c: Coincident(g278,g267)
    c: Coincident(g279,g280)
    c: Coincident(g280,g281)
    c: Coincident(g281,g282)
    c: Coincident(g282,g283)
    c: Coincident(g283,g284)
    c: Coincident(g284,g285)
    c: Coincident(g285,g286)
    c: Coincident(g286,g287)
    c: Coincident(g287,g279)
    c: Coincident(g288,g289)
    c: Coincident(g289,g290)
    c: Coincident(g290,g291)
    c: Coincident(g291,g292)
    c: Coincident(g292,g293)
    c: Coincident(g293,g294)
    c: Coincident(g294,g295)
    c: Coincident(g295,g296)
    c: Coincident(g296,g297)
    c: Coincident(g297,g298)
    c: Coincident(g298,g299)
    c: Coincident(g299,g300)
    c: Coincident(g300,g301)
    c: Coincident(g301,g302)
    c: Coincident(g302,g303)
    c: Coincident(g303,g304)
    c: Coincident(g304,g305)
    c: Coincident(g305,g288)
    c: Coincident(g306,g307)
    c: Coincident(g307,g308)
    c: Coincident(g308,g309)
    c: Coincident(g309,g310)
    c: Coincident(g310,g311)
    c: Coincident(g311,g312)
    c: Coincident(g312,g313)
    c: Coincident(g313,g314)
    c: Coincident(g314,g315)
    c: Coincident(g315,g316)
    c: Coincident(g316,g317)
    c: Coincident(g317,g318)
    c: Coincident(g318,g319)
    c: Coincident(g319,g320)
    c: Coincident(g320,g321)
    c: Coincident(g321,g322)
    c: Coincident(g322,g323)
    c: Coincident(g323,g324)
    c: Coincident(g324,g325)
    c: Coincident(g325,g326)
    c: Coincident(g326,g327)
    c: Coincident(g327,g306)
    c: Coincident(g328,g329)
    c: Coincident(g329,g330)
    c: Coincident(g330,g331)
    c: Coincident(g331,g332)
    c: Coincident(g332,g333)
    c: Coincident(g333,g334)
    c: Coincident(g334,g335)
    c: Coincident(g335,g336)
    c: Coincident(g336,g337)
    c: Coincident(g337,g338)
    c: Coincident(g338,g339)
    c: Coincident(g339,g328)
    c: Coincident(g340,g341)
    c: Coincident(g341,g342)
    c: Coincident(g342,g343)
    c: Coincident(g343,g344)
    c: Coincident(g344,g345)
    c: Coincident(g345,g346)
    c: Coincident(g346,g347)
    c: Coincident(g347,g340)
FEATURE [Sketcher::SketchObject] Sketch
  MapMode = 5
  Support = -> [XY_Plane]
  sketch-geometry (5):
    g0: LineSegment StartX=-25 StartY=25 StartZ=0 EndX=-25 EndY=-25 EndZ=0
    g1: LineSegment StartX=-25 StartY=-25 StartZ=0 EndX=25 EndY=-25 EndZ=0
    g2: LineSegment StartX=25 StartY=-25 StartZ=0 EndX=25 EndY=25 EndZ=0
    g3: LineSegment StartX=25 StartY=25 StartZ=0 EndX=-25 EndY=25 EndZ=0
    g4: Circle [constr] CenterX=0 CenterY=0 CenterZ=0 NormalX=0 NormalY=0 NormalZ=1 AngleXU=0 Radius=35.3553
  constraints (14):
    c: Coincident(g0,g1)
    c: Coincident(g1,g2)
    c: Coincident(g2,g3)
    c: Coincident(g3,g0)
    c: Equal(g0,g1)
    c: Equal(g0,g2)
    c: Equal(g0,g3)
    c: PointOnObject(g0,g4)
    c: PointOnObject(g1,g4)
    c: PointOnObject(g2,g4)
    c: PointOnObject(g3,g4)
    c: Coincident(g4,g-1)
    c: Horizontal(g3)
    c: DistanceX(g3,g3) = 50
FEATURE [PartDesign::Pad] Pad
  Length = 1.5
  Length2 = 100
  Profile = -> Sketch
  Type = 0
FEATURE [PartDesign::Pad] Pad001
  BaseFeature = -> Pad
  Length = 1.5
  Length2 = 100
  Profile = -> Sketch018
  Reversed = true
  Type = 0
FEATURE [PartDesign::Body] Body
  Group = -> [Sketch018,Sketch,Pad,Pad001]
  Origin = -> Origin
  Tip = -> Pad001
